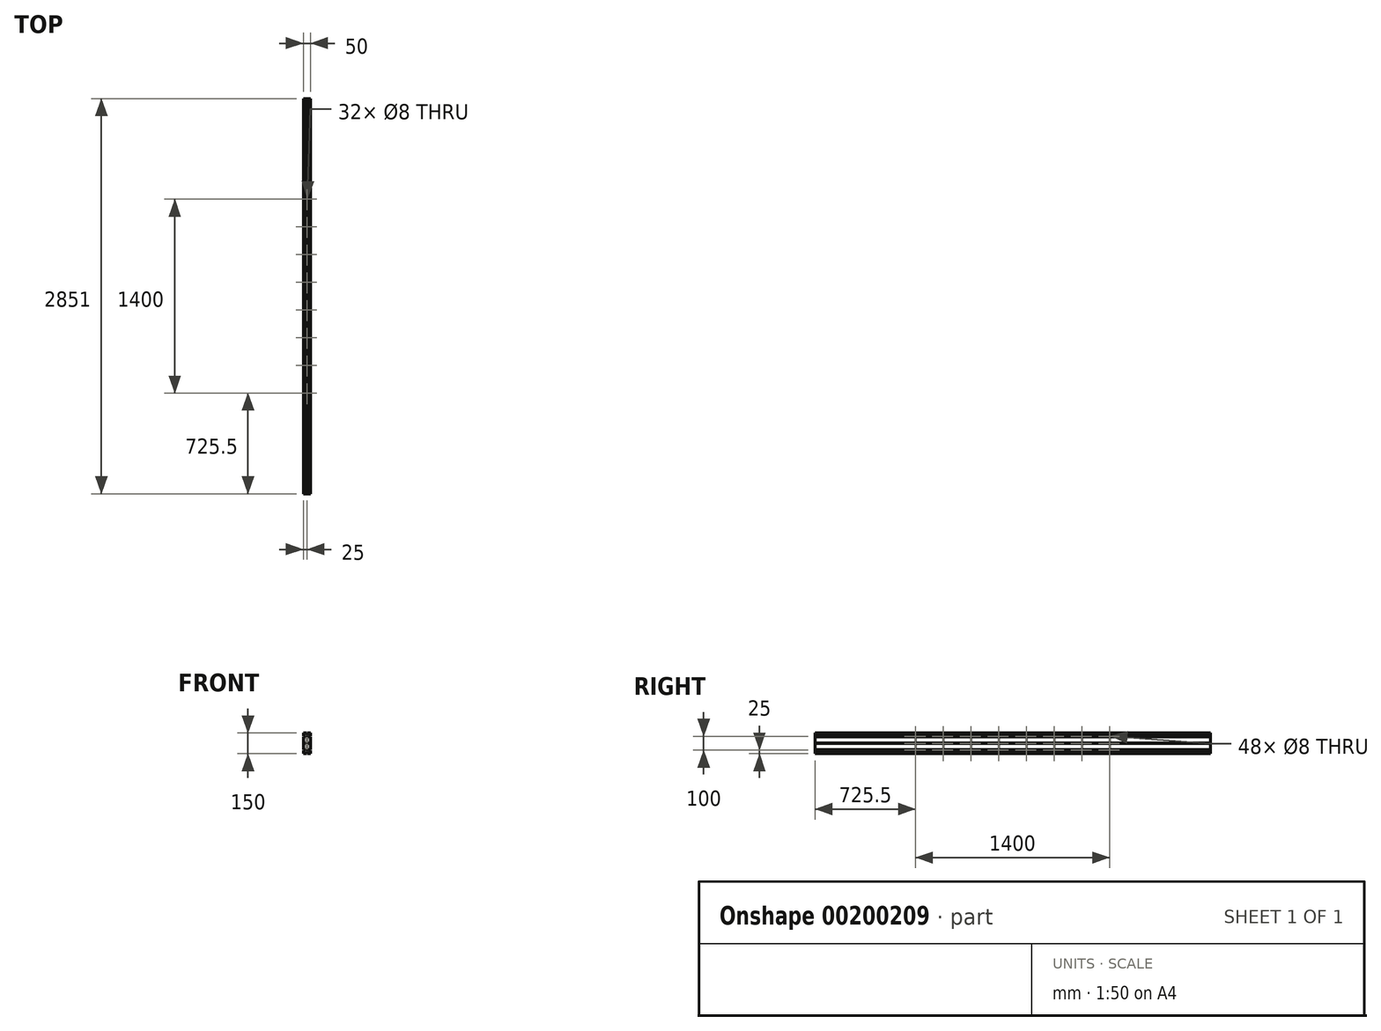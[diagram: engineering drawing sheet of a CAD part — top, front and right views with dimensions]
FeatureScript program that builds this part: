
annotation { "Feature Type Name" : "Feature", "Feature Type Description" : "" }
export const myFeature = defineFeature(function(context is Context, id is Id, definition is map)
    precondition{}
    {
        {
            var Q0;
            Q0=qCreatedBy(makeId("Front.planeOp"),FACE);
            var sketch = newSketch(context, id + "F0", { "sketchPlane" : qUnion([Q0])});
            skLineSegment(sketch, "E0.bottom", {"start": v(25, -75) * mm, "end": v(-25, -75) * mm});
            skLineSegment(sketch, "E0.top", {"start": v(25, 75) * mm, "end": v(-25, 75) * mm});
            skLineSegment(sketch, "E0.left", {"start": v(25, -75) * mm, "end": v(25, 75) * mm});
            skLineSegment(sketch, "E0.right", {"start": v(-25, -75) * mm, "end": v(-25, 75) * mm});
            skPoint(sketch, "E0.middle", {"position": v(0, 0) * mm});
            skSolve(sketch);
        }
        {
            var Q0;
            Q0=qSketchRegion(id+"F0",true);
            extrude(context, id + "F1", {"entities" : qUnion([Q0]), "depth" : 2851 * mm});
        }
        {
            var Q0;
            Q0=makeQuery(id+"F1.opExtrude","SWEPT_FACE",FACE,{"disambiguationData":[OSD([sQuery(id+"F0.wireOp",EDGE,"E0.left")])]});
            var sketch = newSketch(context, id + "F2", { "sketchPlane" : qUnion([Q0])});
            skLineSegment(sketch, "E1", {"start": v(-2851, 0) * mm, "end": v(-640.44, 0) * mm, "construction": true});
            skCircle(sketch, "E2", {"center": v(-2125.5, 50) * mm, "radius": 4 * mm});
            skCircle(sketch, "E3.1.0.0", {"center": v(-1925.5, 50) * mm, "radius": 4 * mm});
            skCircle(sketch, "E3.2.0.0", {"center": v(-1725.5, 50) * mm, "radius": 4 * mm});
            skCircle(sketch, "E3.3.0.0", {"center": v(-1525.5, 50) * mm, "radius": 4 * mm});
            skCircle(sketch, "E3.4.0.0", {"center": v(-1325.5, 50) * mm, "radius": 4 * mm});
            skLineSegment(sketch, "E3.direction1", {"start": v(-2125.5, 50) * mm, "end": v(-1925.5, 50) * mm, "construction": true});
            skCircle(sketch, "E4.0.5.0", {"center": v(-1125.5, 50) * mm, "radius": 4 * mm});
            skCircle(sketch, "E4.0.6.0", {"center": v(-925.5, 50) * mm, "radius": 4 * mm});
            skCircle(sketch, "E4.0.7.0", {"center": v(-725.5, 50) * mm, "radius": 4 * mm});
            skCircle(sketch, "E5.MirrorC", {"center": v(-1925.5, -50) * mm, "radius": 4 * mm});
            skCircle(sketch, "E6.MirrorC", {"center": v(-1725.5, -50) * mm, "radius": 4 * mm});
            skCircle(sketch, "E7.MirrorC", {"center": v(-1525.5, -50) * mm, "radius": 4 * mm});
            skCircle(sketch, "E8.MirrorC", {"center": v(-725.5, -50) * mm, "radius": 4 * mm});
            skCircle(sketch, "E9.MirrorC", {"center": v(-925.5, -50) * mm, "radius": 4 * mm});
            skCircle(sketch, "E10.MirrorC", {"center": v(-1325.5, -50) * mm, "radius": 4 * mm});
            skCircle(sketch, "E11.MirrorC", {"center": v(-1125.5, -50) * mm, "radius": 4 * mm});
            skCircle(sketch, "E12.MirrorC", {"center": v(-2125.5, -50) * mm, "radius": 4 * mm});
            skCircle(sketch, "E13", {"center": v(-2125.5, 0) * mm, "radius": 4 * mm});
            skCircle(sketch, "E14.1.0.0", {"center": v(-1925.5, 0) * mm, "radius": 4 * mm});
            skCircle(sketch, "E14.2.0.0", {"center": v(-1725.5, 0) * mm, "radius": 4 * mm});
            skLineSegment(sketch, "E14.direction1", {"start": v(-2125.5, 0) * mm, "end": v(-1925.5, 0) * mm, "construction": true});
            skCircle(sketch, "E15.0.3.0", {"center": v(-1525.5, 0) * mm, "radius": 4 * mm});
            skCircle(sketch, "E15.0.4.0", {"center": v(-1325.5, 0) * mm, "radius": 4 * mm});
            skCircle(sketch, "E15.0.5.0", {"center": v(-1125.5, 0) * mm, "radius": 4 * mm});
            skCircle(sketch, "E15.0.6.0", {"center": v(-925.5, 0) * mm, "radius": 4 * mm});
            skCircle(sketch, "E15.0.7.0", {"center": v(-725.5, 0) * mm, "radius": 4 * mm});
            skLineSegment(sketch, "E16", {"start": v(-1525.5, 50) * mm, "end": v(-1325.5, 50) * mm, "construction": true});
            skLineSegment(sketch, "E17", {"start": v(-1425.5, 50) * mm, "end": v(-1425.5, -75) * mm, "construction": true});
            skLineSegment(sketch, "E18", {"start": v(-2125.5, 50) * mm, "end": v(-2125.5, 0) * mm, "construction": true});
            skSolve(sketch);
        }
        {
            var Q0;
            Q0=qSketchRegion(id+"F2",true);
            extrude(context, id + "F3", {"entities" : qUnion([Q0]), "operationType" : NewBodyOperationType.REMOVE, "endBound" : BoundingType.THROUGH_ALL, "oppositeDirection" : true, "depth" : 25 * mm});
        }
        {
            var Q0;
            Q0=makeQuery(id+"F1.opExtrude","SWEPT_FACE",FACE,{"disambiguationData":[OSD([sQuery(id+"F0.wireOp",EDGE,"E0.bottom")])]});
            var sketch = newSketch(context, id + "F4", { "sketchPlane" : qUnion([Q0])});
            skLineSegment(sketch, "E19", {"start": v(0, 2851) * mm, "end": v(0, 1392.8) * mm, "construction": true});
            skCircle(sketch, "E20", {"center": v(0, 2125.5) * mm, "radius": 4 * mm});
            skCircle(sketch, "E21.0.1.0", {"center": v(0, 1925.5) * mm, "radius": 4 * mm});
            skCircle(sketch, "E21.0.2.0", {"center": v(0, 1725.5) * mm, "radius": 4 * mm});
            skCircle(sketch, "E21.0.3.0", {"center": v(0, 1525.5) * mm, "radius": 4 * mm});
            skCircle(sketch, "E21.0.4.0", {"center": v(0, 1325.5) * mm, "radius": 4 * mm});
            skCircle(sketch, "E21.0.5.0", {"center": v(0, 1125.5) * mm, "radius": 4 * mm});
            skCircle(sketch, "E21.0.6.0", {"center": v(0, 925.5) * mm, "radius": 4 * mm});
            skCircle(sketch, "E21.0.7.0", {"center": v(0, 725.5) * mm, "radius": 4 * mm});
            skLineSegment(sketch, "E21.direction1", {"start": v(0, 2125.5) * mm, "end": v(25, 2125.5) * mm, "construction": true});
            skLineSegment(sketch, "E21.direction2", {"start": v(0, 2125.5) * mm, "end": v(0, 1925.5) * mm, "construction": true});
            skLineSegment(sketch, "E22", {"start": v(0, 1525.5) * mm, "end": v(0, 1325.5) * mm, "construction": true});
            skLineSegment(sketch, "E23", {"start": v(0, 1425.5) * mm, "end": v(25, 1425.5) * mm, "construction": true});
            skPoint(sketch, "E23.endSnap0", {"position": v(0, 1425.5) * mm});
            skSolve(sketch);
        }
        {
            var Q0;
            Q0=qSketchRegion(id+"F4",true);
            extrude(context, id + "F5", {"entities" : qUnion([Q0]), "operationType" : NewBodyOperationType.REMOVE, "endBound" : BoundingType.THROUGH_ALL, "oppositeDirection" : true, "depth" : 25 * mm});
        }
        {
            var Q0;
            Q0=makeQuery(id+"F1.opExtrude","CAP_FACE",FACE,{"disambiguationData":[OSD([sQuery(id+"F0.wireOp",EDGE,"E0.bottom"),sQuery(id+"F0.wireOp",EDGE,"E0.top"),sQuery(id+"F0.wireOp",EDGE,"E0.left"),sQuery(id+"F0.wireOp",EDGE,"E0.right")])],"isStart":false});
            var sketch = newSketch(context, id + "F6", { "sketchPlane" : qUnion([Q0])});
            skLineSegment(sketch, "E24", {"start": v(0, 75) * mm, "end": v(0, -75) * mm, "construction": true});
            skLineSegment(sketch, "E25", {"start": v(-25, 50) * mm, "end": v(25, 50) * mm, "construction": true});
            skLineSegment(sketch, "E26.bottom", {"start": v(3, 61) * mm, "end": v(-3, 61) * mm});
            skLineSegment(sketch, "E26.top", {"start": v(3, 75) * mm, "end": v(-3, 75) * mm});
            skLineSegment(sketch, "E26.left", {"start": v(3, 61) * mm, "end": v(3, 75) * mm});
            skLineSegment(sketch, "E26.right", {"start": v(-3, 61) * mm, "end": v(-3, 75) * mm});
            skPoint(sketch, "E26.middle", {"position": v(0, 68) * mm});
            skLineSegment(sketch, "E27", {"start": v(-25, 0) * mm, "end": v(25, 0) * mm, "construction": true});
            skLineSegment(sketch, "E28.MirrorCS", {"start": v(-3, -61) * mm, "end": v(-3, -75) * mm});
            skLineSegment(sketch, "E29.MirrorCS", {"start": v(3, -75) * mm, "end": v(-3, -75) * mm});
            skLineSegment(sketch, "E30.MirrorCS", {"start": v(3, -61) * mm, "end": v(3, -75) * mm});
            skLineSegment(sketch, "E31.MirrorCS", {"start": v(3, -61) * mm, "end": v(-3, -61) * mm});
            skLineSegment(sketch, "E32.bottom", {"start": v(-25, 47) * mm, "end": v(-11, 47) * mm});
            skLineSegment(sketch, "E32.top", {"start": v(-25, 53) * mm, "end": v(-11, 53) * mm});
            skLineSegment(sketch, "E32.left", {"start": v(-25, 47) * mm, "end": v(-25, 53) * mm});
            skLineSegment(sketch, "E32.right", {"start": v(-11, 47) * mm, "end": v(-11, 53) * mm});
            skPoint(sketch, "E32.middle", {"position": v(-18, 50) * mm});
            skLineSegment(sketch, "E33.bottom", {"start": v(-25, -3) * mm, "end": v(-11, -3) * mm});
            skLineSegment(sketch, "E33.top", {"start": v(-25, 3) * mm, "end": v(-11, 3) * mm});
            skLineSegment(sketch, "E33.left", {"start": v(-25, -3) * mm, "end": v(-25, 3) * mm});
            skLineSegment(sketch, "E33.right", {"start": v(-11, -3) * mm, "end": v(-11, 3) * mm});
            skPoint(sketch, "E33.middle", {"position": v(-18, 0) * mm});
            skLineSegment(sketch, "E34.MirrorCS", {"start": v(-25, -47) * mm, "end": v(-11, -47) * mm});
            skLineSegment(sketch, "E35.MirrorCS", {"start": v(-25, -53) * mm, "end": v(-11, -53) * mm});
            skLineSegment(sketch, "E36.MirrorCS", {"start": v(-11, -47) * mm, "end": v(-11, -53) * mm});
            skLineSegment(sketch, "E37.MirrorCS", {"start": v(-25, -47) * mm, "end": v(-25, -53) * mm});
            skLineSegment(sketch, "E38.MirrorCS", {"start": v(25, 47) * mm, "end": v(11, 47) * mm});
            skLineSegment(sketch, "E39.MirrorCS", {"start": v(25, 53) * mm, "end": v(11, 53) * mm});
            skLineSegment(sketch, "E40.MirrorCS", {"start": v(11, 47) * mm, "end": v(11, 53) * mm});
            skLineSegment(sketch, "E41.MirrorCS", {"start": v(25, 47) * mm, "end": v(25, 53) * mm});
            skLineSegment(sketch, "E42.MirrorCS", {"start": v(25, -3) * mm, "end": v(11, -3) * mm});
            skLineSegment(sketch, "E43.MirrorCS", {"start": v(25, 3) * mm, "end": v(11, 3) * mm});
            skLineSegment(sketch, "E44.MirrorCS", {"start": v(11, -3) * mm, "end": v(11, 3) * mm});
            skLineSegment(sketch, "E45.MirrorCS", {"start": v(25, -3) * mm, "end": v(25, 3) * mm});
            skLineSegment(sketch, "E46.MirrorCS", {"start": v(25, -47) * mm, "end": v(11, -47) * mm});
            skLineSegment(sketch, "E47.MirrorCS", {"start": v(25, -53) * mm, "end": v(11, -53) * mm});
            skLineSegment(sketch, "E48.MirrorCS", {"start": v(11, -47) * mm, "end": v(11, -53) * mm});
            skLineSegment(sketch, "E49.MirrorCS", {"start": v(25, -47) * mm, "end": v(25, -53) * mm});
            skSolve(sketch);
        }
        {
            var Q0;
            Q0=qSketchRegion(id+"F6",true);
            extrude(context, id + "F7", {"entities" : qUnion([Q0]), "operationType" : NewBodyOperationType.REMOVE, "endBound" : BoundingType.THROUGH_ALL, "oppositeDirection" : true, "depth" : 25 * mm});
        }
    });
